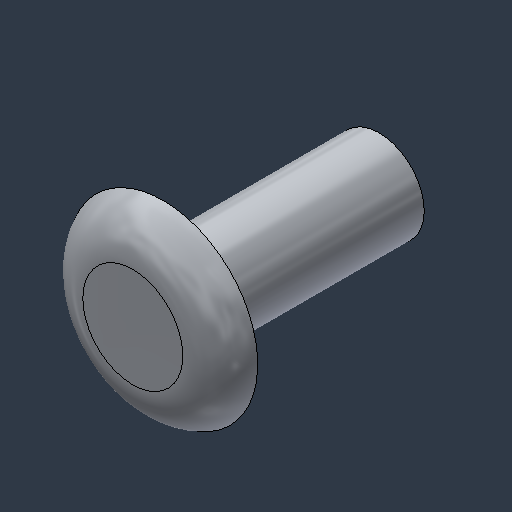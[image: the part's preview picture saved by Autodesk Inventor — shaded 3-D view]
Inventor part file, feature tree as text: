
AUTODESK INVENTOR PART (.ipt)
format: ipt  version: 2024.3 (Build 283343000, 343)  size: 123,904 bytes
history: native  units: mm (DEFAULTED — no unit token found)
features: fillet x1
ambient origin geometry x8: Origin, YZ Plane, XZ Plane, XY Plane, X Axis, Y Axis, Z Axis, Center Point
bodies: Solid1 (feature_tree)
feature tree (1):
  fillet  "Fillet1"  [1 undecoded]
note: 1 required parameter value undecoded (feature->parameter linkage not recoverable at this tier; creation-order binding heuristic only, values carry confidence <= 0.55)
